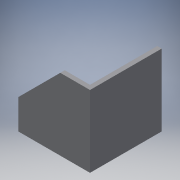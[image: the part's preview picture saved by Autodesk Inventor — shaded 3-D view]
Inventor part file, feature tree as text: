
AUTODESK INVENTOR PART (.ipt)
format: ipt  version: 2016 (Build 200138000, 138)  size: 132,608 bytes
history: native  units: in
note: dims shown in document units (in); Inventor stores cm internally (conversion verified against a paired STEP export)
features: extrude x4, sketch x4
ambient origin geometry x8: Origin, YZ Plane, XZ Plane, XY Plane, X Axis, Y Axis, Z Axis, Center Point
bodies: Solid1 (feature_tree)
feature tree (8):
  extrude  "Extrusion1"  Depth=2.0in
  extrude  "Extrusion2"  TaperAngle=135.0deg  [1 undecoded]
  extrude  "Extrusion3"  Depth=0.125in
  extrude  "Extrusion4"  Depth=0.125in
  sketch  "Sketch1"  dims[d0=2.0in d2=2.0in]
  sketch  "Sketch2"  dims[d3=2.0in d4=135.0deg]
  sketch  "Sketch3"  dims[d5=0.125in d6=0.0in d7=0.125in]
  sketch  "Sketch4"  dims[d8=2.0in d9=0.0in d10=0.2656in d11=0.2656in d12=0.546in d13=0.546in d14=0.5in d15=1.0in d16=0.125in d17=0.0in d18=0.656in d19=0.5in d20=0.5in d21=0.2656in d22=1.0in d23=0.125in d24=0.0in]
note: 1 required parameter value undecoded (feature->parameter linkage not recoverable at this tier; creation-order binding heuristic only, values carry confidence <= 0.55)
